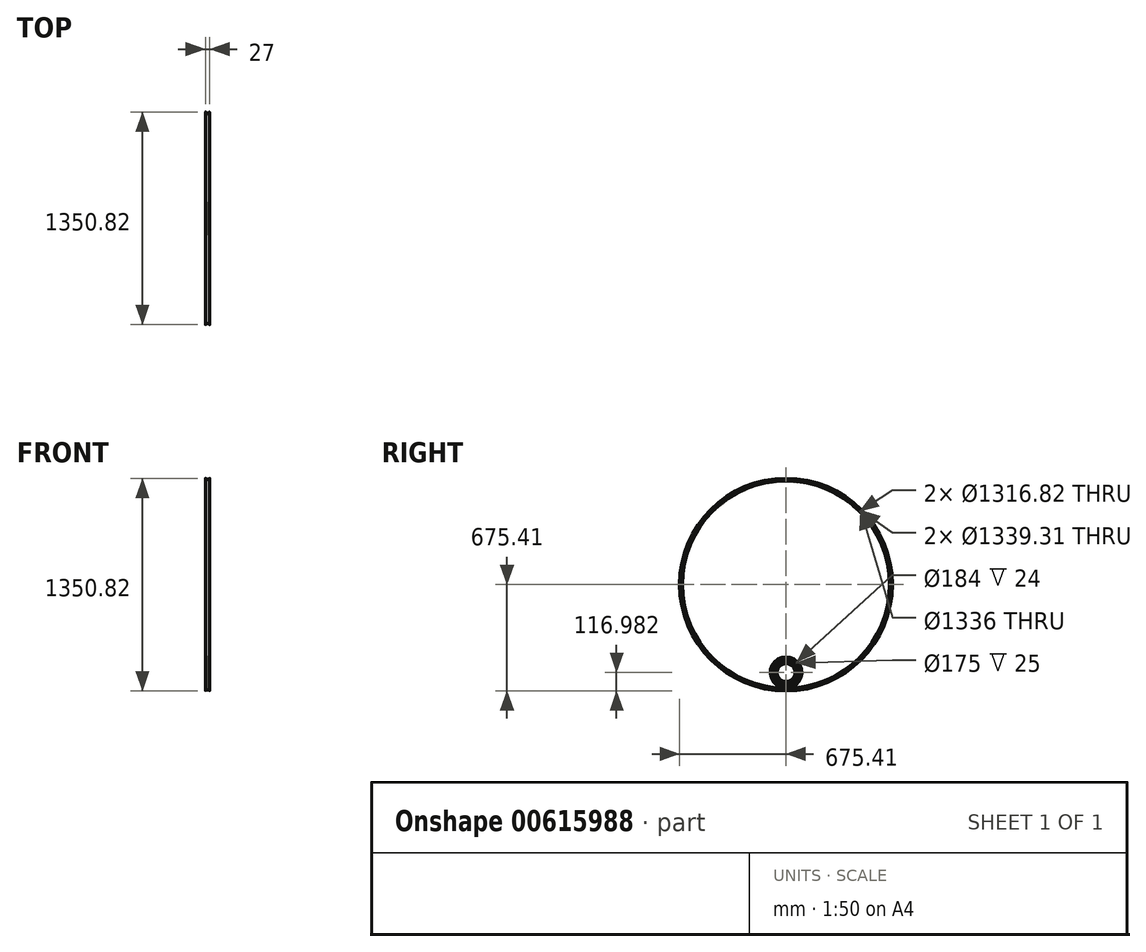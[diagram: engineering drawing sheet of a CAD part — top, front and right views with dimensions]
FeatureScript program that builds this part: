
annotation { "Feature Type Name" : "Feature", "Feature Type Description" : "" }
export const myFeature = defineFeature(function(context is Context, id is Id, definition is map)
    precondition{}
    {
        {
            var Q0;
            Q0=qCreatedBy(makeId("Front.planeOp"),FACE);
            var sketch = newSketch(context, id + "F0", { "sketchPlane" : qUnion([Q0])});
            skLineSegment(sketch, "E0", {"start": v(-12.5, 670.91) * mm, "end": v(-12.5, 673.91) * mm});
            skLineSegment(sketch, "E1", {"start": v(-12, 674.41) * mm, "end": v(-12, 674.41) * mm});
            skLineSegment(sketch, "E2", {"start": v(-11.5, 674.91) * mm, "end": v(-11.5, 674.91) * mm});
            skLineSegment(sketch, "E3", {"start": v(-12, 675.41) * mm, "end": v(-12.5, 675.41) * mm});
            skPoint(sketch, "E4.visualSharp", {"position": v(-11.5, 675.41) * mm});
            skArc(sketch, "E4.filletArc", {"start": v(-11.5, 674.91) * mm, "mid": v(-11.65, 675.27) * mm, "end": v(-12, 675.41) * mm});
            skPoint(sketch, "E5.visualSharp", {"position": v(-11.5, 674.41) * mm});
            skArc(sketch, "E5.filletArc", {"start": v(-12, 674.41) * mm, "mid": v(-11.65, 674.56) * mm, "end": v(-11.5, 674.91) * mm});
            skPoint(sketch, "E6.visualSharp", {"position": v(-12.5, 674.41) * mm});
            skArc(sketch, "E6.filletArc", {"start": v(-12, 674.41) * mm, "mid": v(-12.35, 674.27) * mm, "end": v(-12.5, 673.91) * mm});
            skArc(sketch, "E7.filletArc", {"start": v(-12.5, 670.91) * mm, "mid": v(-12.35, 670.56) * mm, "end": v(-12, 670.41) * mm});
            skLineSegment(sketch, "E8", {"start": v(-12, 670.41) * mm, "end": v(-6.56, 670.41) * mm});
            skLineSegment(sketch, "E9", {"start": v(-5.99, 670.23) * mm, "end": v(-4.49, 669.18) * mm});
            skLineSegment(sketch, "E10", {"start": v(-3.92, 669) * mm, "end": v(0, 669) * mm});
            skPoint(sketch, "E11.visualSharp", {"position": v(-6.25, 670.41) * mm});
            skArc(sketch, "E11.filletArc", {"start": v(-5.99, 670.23) * mm, "mid": v(-6.26, 670.37) * mm, "end": v(-6.56, 670.41) * mm});
            skPoint(sketch, "E12.visualSharp", {"position": v(-4.23, 669) * mm});
            skArc(sketch, "E12.filletArc", {"start": v(-4.49, 669.18) * mm, "mid": v(-4.22, 669.05) * mm, "end": v(-3.92, 669) * mm});
            skLineSegment(sketch, "E13", {"start": v(0, 668) * mm, "end": v(-4.28, 668) * mm});
            skLineSegment(sketch, "E14", {"start": v(-4.85, 668.18) * mm, "end": v(-6.7, 669.48) * mm});
            skLineSegment(sketch, "E15", {"start": v(-7.27, 669.66) * mm, "end": v(-12, 669.66) * mm});
            skLineSegment(sketch, "E16", {"start": v(-12.5, 669.16) * mm, "end": v(-12.5, 660.05) * mm});
            skPoint(sketch, "E17.visualSharp", {"position": v(-12.5, 669.66) * mm});
            skArc(sketch, "E17.filletArc", {"start": v(-12, 669.66) * mm, "mid": v(-12.35, 669.5) * mm, "end": v(-12.5, 669.16) * mm});
            skPoint(sketch, "E18.visualSharp", {"position": v(-6.96, 669.66) * mm});
            skArc(sketch, "E18.filletArc", {"start": v(-6.7, 669.48) * mm, "mid": v(-6.97, 669.61) * mm, "end": v(-7.27, 669.66) * mm});
            skPoint(sketch, "E19.visualSharp", {"position": v(-4.6, 668) * mm});
            skArc(sketch, "E19.filletArc", {"start": v(-4.85, 668.18) * mm, "mid": v(-4.58, 668.05) * mm, "end": v(-4.28, 668) * mm});
            skLineSegment(sketch, "E20", {"start": v(-13.5, 674.41) * mm, "end": v(-13.5, 658.91) * mm});
            skPoint(sketch, "E21.visualSharp", {"position": v(-13.5, 675.41) * mm});
            skArc(sketch, "E21.filletArc", {"start": v(-12.5, 675.41) * mm, "mid": v(-13.2, 675.12) * mm, "end": v(-13.5, 674.41) * mm});
            skLineSegment(sketch, "E22", {"start": v(-13, 658.41) * mm, "end": v(-12.56, 658.41) * mm});
            skArc(sketch, "E23", {"start": v(0, 660) * mm, "mid": v(-6.27, 659.6) * mm, "end": v(-12.44, 658.43) * mm});
            skLineSegment(sketch, "E24", {"start": v(-12.5, 660.05) * mm, "end": v(-12.5, 660.05) * mm});
            skArc(sketch, "E25", {"start": v(0, 661) * mm, "mid": v(-5.98, 660.64) * mm, "end": v(-11.88, 659.57) * mm});
            skPoint(sketch, "E26.visualSharp", {"position": v(-12.5, 659.41) * mm});
            skArc(sketch, "E26.filletArc", {"start": v(-12.5, 660.05) * mm, "mid": v(-12.3, 659.66) * mm, "end": v(-11.88, 659.57) * mm});
            skPoint(sketch, "E27.visualSharp", {"position": v(-13.5, 658.41) * mm});
            skArc(sketch, "E27.filletArc", {"start": v(-13.5, 658.91) * mm, "mid": v(-13.35, 658.56) * mm, "end": v(-13, 658.41) * mm});
            skPoint(sketch, "E28.visualSharp", {"position": v(-12.5, 658.41) * mm});
            skArc(sketch, "E28.filletArc", {"start": v(-12.56, 658.41) * mm, "mid": v(-12.5, 658.42) * mm, "end": v(-12.44, 658.43) * mm});
            skArc(sketch, "E29.MirrorCS", {"start": v(6.7, 669.48) * mm, "mid": v(6.97, 669.61) * mm, "end": v(7.27, 669.66) * mm});
            skLineSegment(sketch, "E30.MirrorCS", {"start": v(12, 675.41) * mm, "end": v(12.5, 675.41) * mm});
            skArc(sketch, "E31.MirrorCS", {"start": v(12, 669.66) * mm, "mid": v(12.35, 669.5) * mm, "end": v(12.5, 669.16) * mm});
            skArc(sketch, "E32.MirrorCS", {"start": v(12, 674.41) * mm, "mid": v(11.65, 674.56) * mm, "end": v(11.5, 674.91) * mm});
            skArc(sketch, "E33.MirrorCS", {"start": v(12, 674.41) * mm, "mid": v(12.35, 674.27) * mm, "end": v(12.5, 673.91) * mm});
            skArc(sketch, "E34.MirrorCS", {"start": v(11.5, 674.91) * mm, "mid": v(11.65, 675.27) * mm, "end": v(12, 675.41) * mm});
            skArc(sketch, "E35.MirrorCS", {"start": v(12.56, 658.41) * mm, "mid": v(12.5, 658.42) * mm, "end": v(12.44, 658.43) * mm});
            skArc(sketch, "E36.MirrorCS", {"start": v(12.5, 660.05) * mm, "mid": v(12.3, 659.66) * mm, "end": v(11.88, 659.57) * mm});
            skLineSegment(sketch, "E37.MirrorCS", {"start": v(13, 658.41) * mm, "end": v(12.56, 658.41) * mm});
            skArc(sketch, "E38.MirrorCS", {"start": v(4.85, 668.18) * mm, "mid": v(4.58, 668.05) * mm, "end": v(4.28, 668) * mm});
            skArc(sketch, "E39.MirrorCS", {"start": v(13.5, 658.91) * mm, "mid": v(13.35, 658.56) * mm, "end": v(13, 658.41) * mm});
            skArc(sketch, "E40.MirrorCS", {"start": v(12.5, 670.91) * mm, "mid": v(12.35, 670.56) * mm, "end": v(12, 670.41) * mm});
            skLineSegment(sketch, "E41.MirrorCS", {"start": v(5.99, 670.23) * mm, "end": v(4.49, 669.18) * mm});
            skArc(sketch, "E42.MirrorCS", {"start": v(5.99, 670.23) * mm, "mid": v(6.26, 670.37) * mm, "end": v(6.56, 670.41) * mm});
            skArc(sketch, "E43.MirrorCS", {"start": v(4.49, 669.18) * mm, "mid": v(4.22, 669.05) * mm, "end": v(3.92, 669) * mm});
            skArc(sketch, "E44.MirrorCS", {"start": v(12.5, 675.41) * mm, "mid": v(13.2, 675.12) * mm, "end": v(13.5, 674.41) * mm});
            skLineSegment(sketch, "E45.MirrorCS", {"start": v(12.5, 669.16) * mm, "end": v(12.5, 660.05) * mm});
            skLineSegment(sketch, "E46.MirrorCS", {"start": v(4.85, 668.18) * mm, "end": v(6.7, 669.48) * mm});
            skPoint(sketch, "E47.MirrorP", {"position": v(6.96, 669.66) * mm});
            skPoint(sketch, "E48.MirrorP", {"position": v(12.5, 659.41) * mm});
            skPoint(sketch, "E49.MirrorP", {"position": v(12.5, 669.66) * mm});
            skPoint(sketch, "E50.MirrorP", {"position": v(11.5, 674.41) * mm});
            skLineSegment(sketch, "E51.MirrorCS", {"start": v(12.5, 670.91) * mm, "end": v(12.5, 673.91) * mm});
            skPoint(sketch, "E52.MirrorP", {"position": v(13.5, 675.41) * mm});
            skPoint(sketch, "E53.MirrorP", {"position": v(4.6, 668) * mm});
            skArc(sketch, "E54.MirrorCS", {"start": v(0, 660) * mm, "mid": v(6.27, 659.6) * mm, "end": v(12.44, 658.43) * mm});
            skLineSegment(sketch, "E55.MirrorCS", {"start": v(12.5, 660.05) * mm, "end": v(12.5, 660.05) * mm});
            skArc(sketch, "E56.MirrorCS", {"start": v(0, 661) * mm, "mid": v(5.98, 660.64) * mm, "end": v(11.88, 659.57) * mm});
            skPoint(sketch, "E57.MirrorP", {"position": v(12.5, 658.41) * mm});
            skPoint(sketch, "E58.MirrorP", {"position": v(6.25, 670.41) * mm});
            skLineSegment(sketch, "E59.MirrorCS", {"start": v(13.5, 674.41) * mm, "end": v(13.5, 658.91) * mm});
            skLineSegment(sketch, "E60.MirrorCS", {"start": v(7.27, 669.66) * mm, "end": v(12, 669.66) * mm});
            skPoint(sketch, "E61.MirrorP", {"position": v(13.5, 658.41) * mm});
            skLineSegment(sketch, "E62.MirrorCS", {"start": v(12, 670.41) * mm, "end": v(6.56, 670.41) * mm});
            skLineSegment(sketch, "E63.MirrorCS", {"start": v(3.92, 669) * mm, "end": v(0, 669) * mm});
            skLineSegment(sketch, "E64.MirrorCS", {"start": v(0, 668) * mm, "end": v(4.28, 668) * mm});
            skPoint(sketch, "E65.MirrorP", {"position": v(4.23, 669) * mm});
            skPoint(sketch, "E66.MirrorP", {"position": v(11.5, 675.41) * mm});
            skLineSegment(sketch, "E67", {"start": v(-88.75, 0) * mm, "end": v(84.03, 0) * mm, "construction": true});
            skSolve(sketch);
        }
        {
            var Q0;
            Q0 = qSketchRegion(id + "F0", true);
            var Q1;
            Q1=sQuery(id+"F0.wireOp",EDGE,"E67");
            revolve(context, id + "F1", {"entities" : qUnion([Q0]), "axis" : qUnion([Q1]), "revolveType" : RevolveType.FULL});
        }
        {
            var Q0;
            Q0=qCreatedBy(makeId("Right.planeOp"),FACE);
            var sketch = newSketch(context, id + "F2", { "sketchPlane" : qUnion([Q0])});
            skCircle(sketch, "E68", {"center": v(-526.91, 304.21) * mm, "radius": 50 * mm, "construction": true});
            skCircle(sketch, "E69", {"center": v(0, -558.43) * mm, "radius": 100 * mm, "construction": true});
            skCircle(sketch, "E70", {"center": v(526.91, 304.21) * mm, "radius": 50 * mm, "construction": true});
            skCircle(sketch, "E71", {"center": v(0, 0) * mm, "radius": 658.43 * mm, "construction": true});
            skLineSegment(sketch, "E72", {"start": v(-526.91, 304.21) * mm, "end": v(0, 0) * mm, "construction": true});
            skLineSegment(sketch, "E73", {"start": v(526.91, 304.21) * mm, "end": v(0, 0) * mm, "construction": true});
            skLineSegment(sketch, "E74", {"start": v(0, -558.43) * mm, "end": v(0, 0) * mm, "construction": true});
            skSolve(sketch);
        }
        {
            var Q0;
            Q0=qCreatedBy(makeId("Front.planeOp"),FACE);
            var sketch = newSketch(context, id + "F3", { "sketchPlane" : qUnion([Q0])});
            skLineSegment(sketch, "E75", {"start": v(-12, -462.43) * mm, "end": v(-12, -466.43) * mm});
            skLineSegment(sketch, "E76", {"start": v(-12, -466.43) * mm, "end": v(0, -466.43) * mm});
            skLineSegment(sketch, "E77.MirrorCS", {"start": v(12, -466.43) * mm, "end": v(0, -466.43) * mm});
            skLineSegment(sketch, "E78.MirrorCS", {"start": v(12, -462.43) * mm, "end": v(12, -466.43) * mm});
            skLineSegment(sketch, "E79", {"start": v(-57.85, -558.43) * mm, "end": v(66.48, -558.43) * mm, "construction": true});
            skArc(sketch, "E80", {"start": v(12, -462.43) * mm, "mid": v(0, -458.43) * mm, "end": v(-12, -462.43) * mm});
            skSolve(sketch);
        }
        {
            var Q0;
            Q0 = qSketchRegion(id + "F3", true);
            var Q1;
            Q1=sQuery(id+"F3.wireOp",EDGE,"E79");
            revolve(context, id + "F4", {"entities" : qUnion([Q0]), "axis" : qUnion([Q1]), "revolveType" : RevolveType.FULL});
        }
        {
            var Q0;
            Q0=qCreatedBy(makeId("Right.planeOp"),FACE);
            var sketch = newSketch(context, id + "F5", { "sketchPlane" : qUnion([Q0])});
            skCircle(sketch, "E81", {"center": v(0, -558.43) * mm, "radius": 92 * mm});
            skCircle(sketch, "E82", {"center": v(0, -558.43) * mm, "radius": 87.5 * mm});
            skSolve(sketch);
        }
        {
            var Q0;
            Q0 = qSketchRegion(id + "F5", true);
            extrude(context, id + "F6", {"entities" : qUnion([Q0]), "endBound" : BoundingType.SYMMETRIC, "depth" : 25 * mm, "offsetDistance" : 25 * mm});
        }
        {
            var Q0;
            Q0=qCreatedBy(makeId("Right.planeOp"),FACE);
            var sketch = newSketch(context, id + "F7", { "sketchPlane" : qUnion([Q0])});
            skArc(sketch, "E83", {"start": v(11.57, -471.7) * mm, "mid": v(0, -470.93) * mm, "end": v(-11.57, -471.7) * mm});
            skArc(sketch, "E84", {"start": v(11.43, -475.67) * mm, "mid": v(0, -474.89) * mm, "end": v(-11.43, -475.67) * mm});
            skLineSegment(sketch, "E85", {"start": v(12, -472.2) * mm, "end": v(12, -475.18) * mm});
            skLineSegment(sketch, "E86", {"start": v(-12, -472.2) * mm, "end": v(-12, -475.18) * mm});
            skPoint(sketch, "E87.visualSharp", {"position": v(12, -475.75) * mm});
            skArc(sketch, "E87.filletArc", {"start": v(11.43, -475.67) * mm, "mid": v(11.83, -475.56) * mm, "end": v(12, -475.18) * mm});
            skPoint(sketch, "E88.visualSharp", {"position": v(12, -471.75) * mm});
            skArc(sketch, "E88.filletArc", {"start": v(12, -472.2) * mm, "mid": v(11.88, -471.86) * mm, "end": v(11.57, -471.7) * mm});
            skPoint(sketch, "E89.visualSharp", {"position": v(-12, -475.75) * mm});
            skArc(sketch, "E89.filletArc", {"start": v(-12, -475.18) * mm, "mid": v(-11.83, -475.56) * mm, "end": v(-11.43, -475.67) * mm});
            skPoint(sketch, "E90.visualSharp", {"position": v(-12, -471.75) * mm});
            skArc(sketch, "E90.filletArc", {"start": v(-11.57, -471.7) * mm, "mid": v(-11.88, -471.86) * mm, "end": v(-12, -472.2) * mm});
            skSolve(sketch);
        }
        {
            var Q0;
            Q0 = qSketchRegion(id + "F7", true);
            extrude(context, id + "F8", {"entities" : qUnion([Q0]), "endBound" : BoundingType.SYMMETRIC, "depth" : 22 * mm, "offsetDistance" : 25 * mm});
        }
        {
            var Q0;
            Q0=qCreatedBy(makeId("Front.planeOp"),FACE);
            var sketch = newSketch(context, id + "F9", { "sketchPlane" : qUnion([Q0])});
            skLineSegment(sketch, "E91", {"start": v(43.54, -558.43) * mm, "end": v(-50.66, -558.43) * mm, "construction": true});
            skSolve(sketch);
        }
        {
            var Q0;
            Q0=makeQuery(id+"F8.opExtrude","SWEPT_BODY",BODY,{"disambiguationData":[OSD([sQuery(id+"F7.wireOp",EDGE,"E83"),sQuery(id+"F7.wireOp",EDGE,"E84"),sQuery(id+"F7.wireOp",EDGE,"E85"),sQuery(id+"F7.wireOp",EDGE,"E86"),sQuery(id+"F7.wireOp",EDGE,"E87.filletArc"),sQuery(id+"F7.wireOp",EDGE,"E88.filletArc"),sQuery(id+"F7.wireOp",EDGE,"E89.filletArc"),sQuery(id+"F7.wireOp",EDGE,"E90.filletArc")])]});
            var Q1;
            Q1=sQuery(id+"F9.wireOp",EDGE,"E91");
            circularPattern(context, id + "F10", {"entities" : qUnion([Q0]), "axis" : qUnion([Q1]), "angle" : 360 * degree, "instanceCount" : 16, "equalSpace" : true});
        }
        {
            var Q0;
            Q0=qCreatedBy(makeId("Right.planeOp"),FACE);
            var sketch = newSketch(context, id + "F11", { "sketchPlane" : qUnion([Q0])});
            skLineSegment(sketch, "E92.top", {"start": v(8, -501.43) * mm, "end": v(-8, -501.43) * mm});
            skArc(sketch, "E93", {"start": v(8, -476.43) * mm, "mid": v(0, -475.9) * mm, "end": v(-8, -476.43) * mm});
            skArc(sketch, "E94", {"start": v(8.67, -478.02) * mm, "mid": v(5.05, -488.94) * mm, "end": v(8.8, -499.82) * mm});
            skArc(sketch, "E95", {"start": v(-8.8, -499.82) * mm, "mid": v(-5.05, -488.94) * mm, "end": v(-8.67, -478.02) * mm});
            skPoint(sketch, "E96.visualSharp", {"position": v(9.77, -476.7) * mm});
            skArc(sketch, "E96.filletArc", {"start": v(8.67, -478.02) * mm, "mid": v(8.79, -477.03) * mm, "end": v(8, -476.43) * mm});
            skPoint(sketch, "E97.visualSharp", {"position": v(-9.77, -476.7) * mm});
            skArc(sketch, "E97.filletArc", {"start": v(-8, -476.43) * mm, "mid": v(-8.79, -477.03) * mm, "end": v(-8.67, -478.02) * mm});
            skPoint(sketch, "E98.visualSharp", {"position": v(-10.2, -501.43) * mm});
            skArc(sketch, "E98.filletArc", {"start": v(-8.8, -499.82) * mm, "mid": v(-8.9, -500.87) * mm, "end": v(-8, -501.43) * mm});
            skPoint(sketch, "E99.visualSharp", {"position": v(10.2, -501.43) * mm});
            skArc(sketch, "E99.filletArc", {"start": v(8, -501.43) * mm, "mid": v(8.9, -500.87) * mm, "end": v(8.8, -499.82) * mm});
            skSolve(sketch);
        }
        {
            var Q0;
            Q0 = qSketchRegion(id + "F11", true);
            extrude(context, id + "F12", {"entities" : qUnion([Q0]), "endBound" : BoundingType.SYMMETRIC, "depth" : 15 * mm, "offsetDistance" : 25 * mm});
        }
        {
            var Q0;
            Q0=makeQuery(id+"F12.opExtrude","CAP_EDGE",EDGE,{"disambiguationData":[OSD([sQuery(id+"F11.wireOp",EDGE,"E95")])],"isStart":true});
            var Q1;
            Q1=makeQuery(id+"F12.opExtrude","CAP_EDGE",EDGE,{"disambiguationData":[OSD([sQuery(id+"F11.wireOp",EDGE,"E94")])],"isStart":true});
            var Q2;
            Q2=makeQuery(id+"F12.opExtrude","CAP_EDGE",EDGE,{"disambiguationData":[OSD([sQuery(id+"F11.wireOp",EDGE,"E94")])],"isStart":false});
            var Q3;
            Q3=makeQuery(id+"F12.opExtrude","CAP_EDGE",EDGE,{"disambiguationData":[OSD([sQuery(id+"F11.wireOp",EDGE,"E95")])],"isStart":false});
            fillet(context, id + "F13", {"entities" : qUnion([Q0, Q1, Q2, Q3]), "radius" : 4 * mm, "tangentPropagation" : true, "allowEdgeOverflow" : false});
        }
        {
            var Q0;
            Q0=makeQuery(id+"F12.opExtrude","SWEPT_BODY",BODY,{"disambiguationData":[OSD([sQuery(id+"F11.wireOp",EDGE,"E92.top"),sQuery(id+"F11.wireOp",EDGE,"E93"),sQuery(id+"F11.wireOp",EDGE,"E94"),sQuery(id+"F11.wireOp",EDGE,"E95"),sQuery(id+"F11.wireOp",EDGE,"E96.filletArc"),sQuery(id+"F11.wireOp",EDGE,"E97.filletArc"),sQuery(id+"F11.wireOp",EDGE,"E98.filletArc"),sQuery(id+"F11.wireOp",EDGE,"E99.filletArc")])]});
            var Q1;
            Q1=sQuery(id+"F9.wireOp",EDGE,"E91");
            circularPattern(context, id + "F14", {"entities" : qUnion([Q0]), "axis" : qUnion([Q1]), "angle" : 360 * degree, "instanceCount" : 16, "equalSpace" : true});
        }
    });
